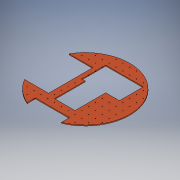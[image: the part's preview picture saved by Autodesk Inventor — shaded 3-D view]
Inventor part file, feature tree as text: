
AUTODESK INVENTOR PART (.ipt)
format: ipt  version: 2018 (Build 220112000, 112)  size: 247,808 bytes
history: native  units: in
note: dims shown in document units (in); Inventor stores cm internally (conversion verified against a paired STEP export)
features: sketch x3, extrude x2, hole x1, pattern_linear x1
ambient origin geometry x8: Origin, YZ Plane, XZ Plane, XY Plane, X Axis, Y Axis, Z Axis, Center Point
bodies: Solid1 (feature_tree)
feature tree (7):
  extrude  "Extrusion1"  Depth=0.125in TaperAngle=0.0deg
  hole  "Hole1"  [1 undecoded]
  pattern_linear  "Rectangular Pattern1"  Spacing1=3.0in  [1 undecoded]
  extrude  "Extrusion2"  Depth=8.0in
  sketch  "Sketch1"  dims[d0=13.0in d1=0.125in d2=0.0in]
  sketch  "Sketch2"  dims[d3=0.085in d4=0.224in d5=0.375in d6=0.25in d7=0.5635in d8=0.349in d9=0.8108in d10=5.1181in d12=1.0in d13=5.1181in d15=1.0in]
  sketch  "Sketch3"  dims[d16=4.5in d17=3.0in d18=8.0in d19=2.0in d20=5.5in d21=3.5in d22=0.5in d23=1.3in d24=5.0in d25=3.0in d26=6.5in d27=5.0in d28=3.5in d30=3.5in d31=0.125in d32=0.0in d34=0.5in d35=180.0deg]
note: 2 required parameter values undecoded (feature->parameter linkage not recoverable at this tier; creation-order binding heuristic only, values carry confidence <= 0.55)
